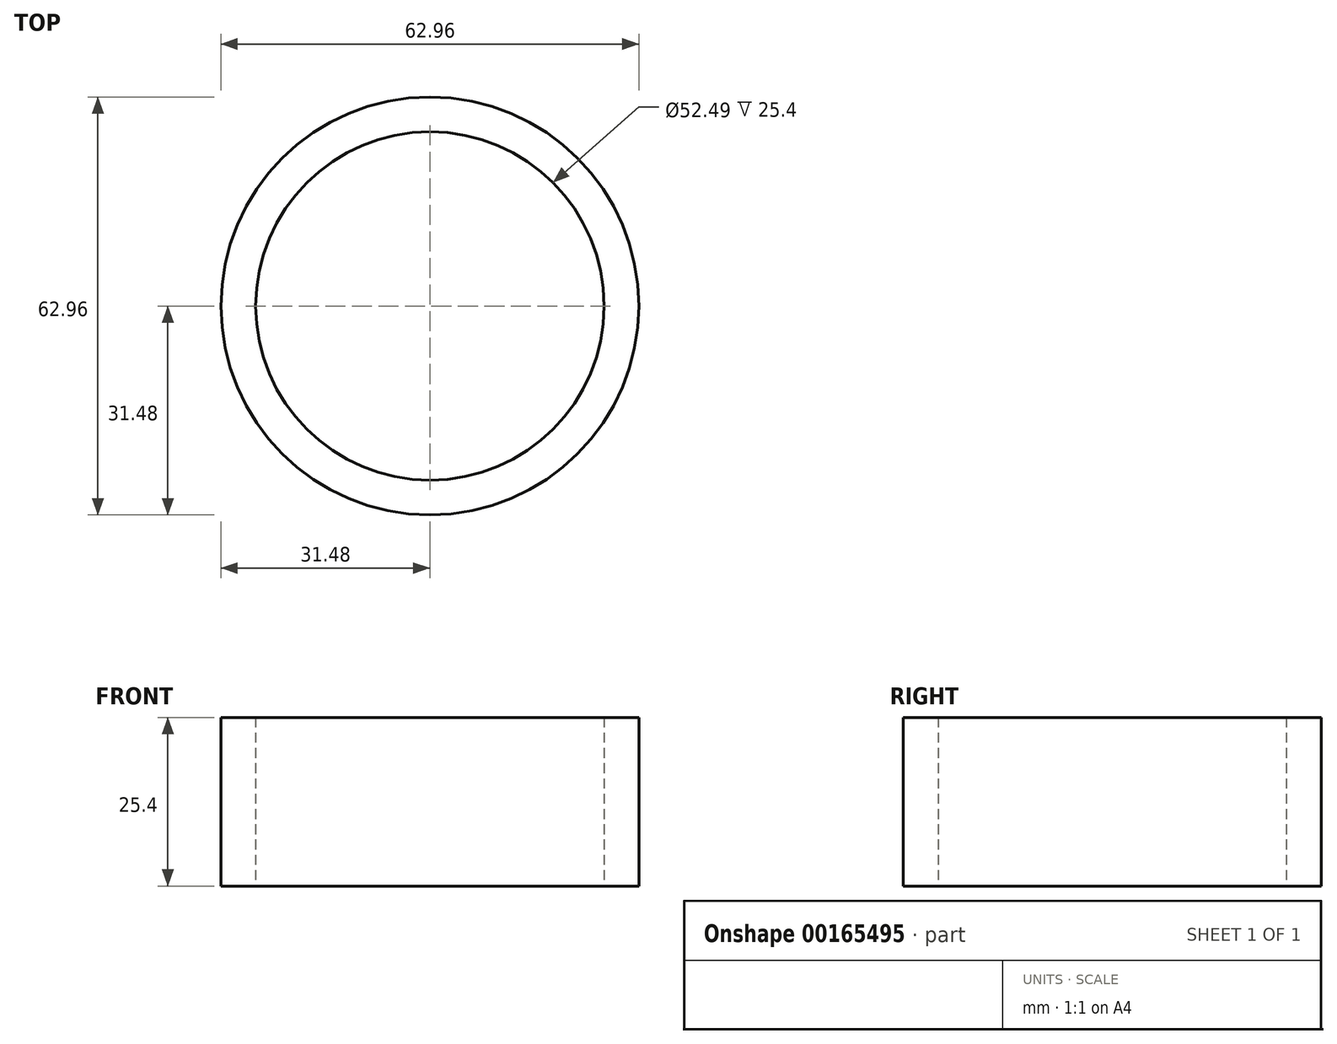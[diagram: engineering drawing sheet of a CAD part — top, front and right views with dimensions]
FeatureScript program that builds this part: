
annotation { "Feature Type Name" : "Feature", "Feature Type Description" : "" }
export const myFeature = defineFeature(function(context is Context, id is Id, definition is map)
    precondition{}
    {
        {
            var Q0;
            Q0=qCreatedBy(makeId("Top.planeOp"),FACE);
            var sketch = newSketch(context, id + "F0", { "sketchPlane" : qUnion([Q0])});
            skCircle(sketch, "E0", {"center": v(0, 0) * mm, "radius": 31.48 * mm});
            skCircle(sketch, "E1", {"center": v(0, 0) * mm, "radius": 26.25 * mm});
            skSolve(sketch);
        }
        {
            var Q0;
            Q0=makeQuery(id+"F0.imprint","IMPRINT",FACE,{"disambiguationData":[TD([[makeQuery(id+"F0.imprint","IMPRINT",EDGE,{"derivedFrom":sQuery(id+"F0.wireOp",EDGE,"E0")}),1.0]])]});
            var Q1;
            Q1=sQuery(id+"F0.wireOp",EDGE,"E0");
            var Q2;
            Q2=sQuery(id+"F0.wireOp",EDGE,"E1");
            extrude(context, id + "F1", {"entities" : qUnion([Q0]), "surfaceEntities" : qUnion([Q1, Q2]), "depth" : 25.4 * mm});
        }
    });
